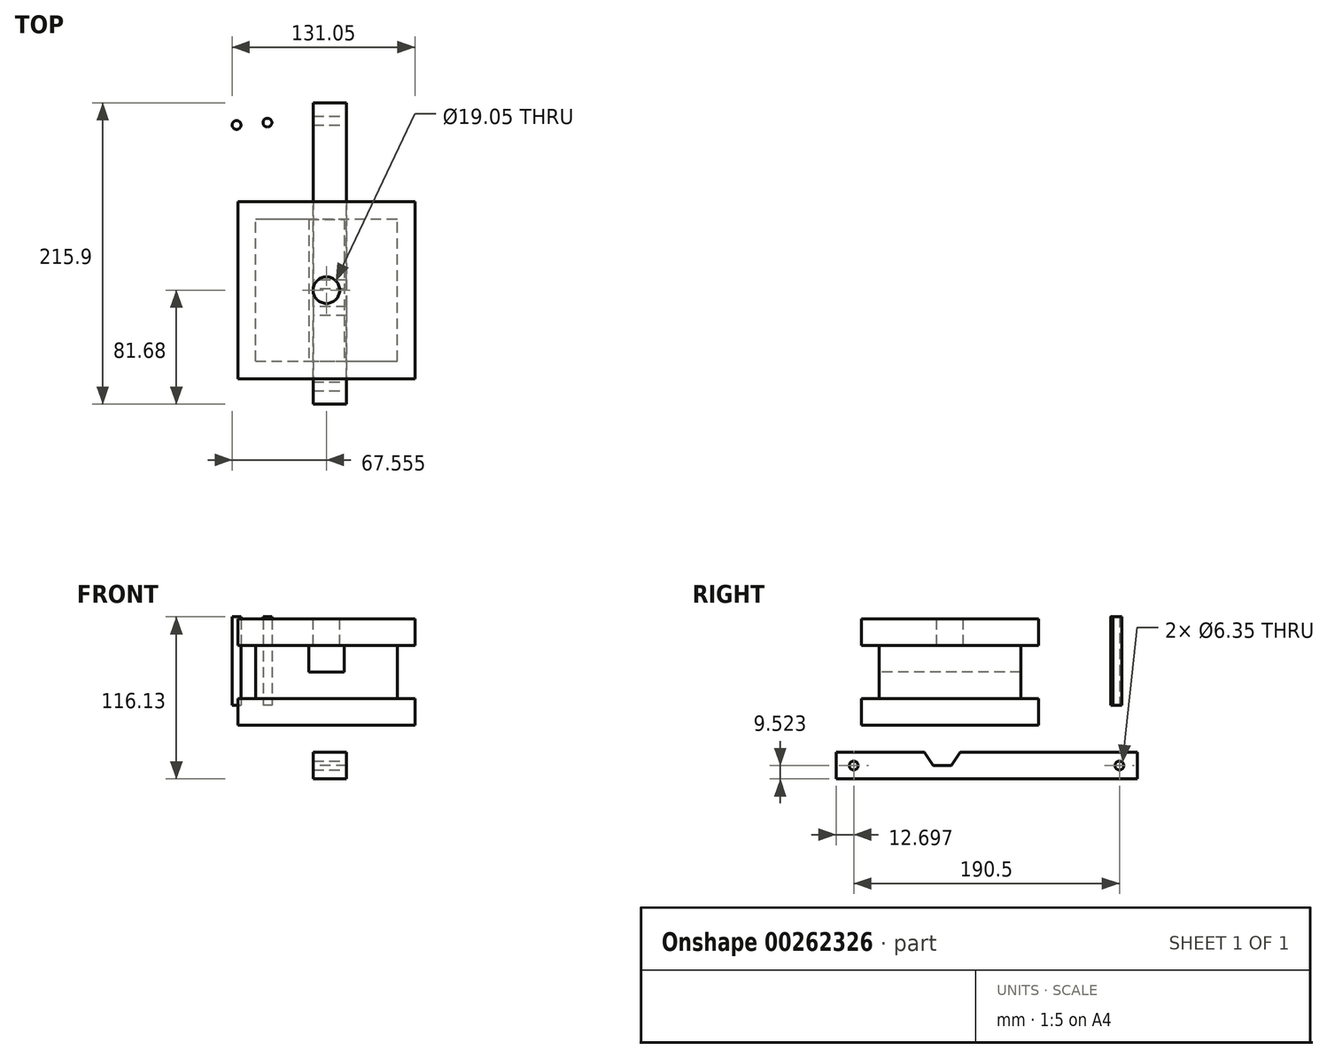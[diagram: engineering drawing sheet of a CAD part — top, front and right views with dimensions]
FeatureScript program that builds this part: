
annotation { "Feature Type Name" : "Feature", "Feature Type Description" : "" }
export const myFeature = defineFeature(function(context is Context, id is Id, definition is map)
    precondition{}
    {
        {
            var Q0;
            Q0=qCreatedBy(makeId("Front.planeOp"),FACE);
            var sketch = newSketch(context, id + "F0", { "sketchPlane" : qUnion([Q0])});
            skLineSegment(sketch, "E0", {"start": v(-54.17, 62.06) * mm, "end": v(72.83, 62.06) * mm});
            skLineSegment(sketch, "E1", {"start": v(72.83, 62.06) * mm, "end": v(72.83, 43) * mm});
            skLineSegment(sketch, "E2", {"start": v(72.83, 4.9) * mm, "end": v(72.83, -14.14) * mm});
            skLineSegment(sketch, "E3", {"start": v(72.83, -14.14) * mm, "end": v(-54.17, -14.14) * mm});
            skLineSegment(sketch, "E4", {"start": v(-54.17, -14.14) * mm, "end": v(-54.17, 4.9) * mm});
            skLineSegment(sketch, "E5", {"start": v(-54.17, 43) * mm, "end": v(-54.17, 62.06) * mm});
            skPoint(sketch, "E6.start.orphan", {"position": v(47.43, 4.9) * mm});
            skLineSegment(sketch, "E7", {"start": v(-54.17, 43) * mm, "end": v(-41.47, 43) * mm});
            skLineSegment(sketch, "E8", {"start": v(-41.47, 43) * mm, "end": v(-41.47, 4.9) * mm});
            skLineSegment(sketch, "E9", {"start": v(-41.47, 4.9) * mm, "end": v(-54.17, 4.9) * mm});
            skLineSegment(sketch, "E10", {"start": v(72.83, 43) * mm, "end": v(60.13, 43) * mm});
            skLineSegment(sketch, "E11", {"start": v(60.13, 43) * mm, "end": v(60.13, 4.9) * mm});
            skLineSegment(sketch, "E12", {"start": v(60.13, 4.9) * mm, "end": v(72.83, 4.9) * mm});
            skSolve(sketch);
        }
        {
            var Q0;
            Q0=makeQuery(id+"F0.imprint","IMPRINT",FACE,{"disambiguationData":[TD([[makeQuery(id+"F0.imprint","IMPRINT",EDGE,{"derivedFrom":sQuery(id+"F0.wireOp",EDGE,"E0")}),-1.0]])]});
            extrude(context, id + "F1", {"entities" : qUnion([Q0]), "depth" : 127 * mm});
        }
        {
            var Q0;
            Q0=makeQuery(id+"F1.opExtrude","CAP_FACE",FACE,{"disambiguationData":[OSD([sQuery(id+"F0.wireOp",EDGE,"E0"),sQuery(id+"F0.wireOp",EDGE,"E1"),sQuery(id+"F0.wireOp",EDGE,"E2"),sQuery(id+"F0.wireOp",EDGE,"E3"),sQuery(id+"F0.wireOp",EDGE,"E4"),sQuery(id+"F0.wireOp",EDGE,"E5"),sQuery(id+"F0.wireOp",EDGE,"E7"),sQuery(id+"F0.wireOp",EDGE,"E8"),sQuery(id+"F0.wireOp",EDGE,"E9"),sQuery(id+"F0.wireOp",EDGE,"E10"),sQuery(id+"F0.wireOp",EDGE,"E11"),sQuery(id+"F0.wireOp",EDGE,"E12")])],"isStart":false});
            var sketch = newSketch(context, id + "F2", { "sketchPlane" : qUnion([Q0])});
            skLineSegment(sketch, "E13", {"start": v(-41.47, 43) * mm, "end": v(60.13, 43) * mm});
            skLineSegment(sketch, "E14", {"start": v(-41.47, 4.9) * mm, "end": v(60.13, 4.9) * mm});
            skSolve(sketch);
        }
        {
            var Q0;
            Q0=makeQuery(id+"F2.imprint","IMPRINT",FACE,{"disambiguationData":[TD([[makeQuery(id+"F2.imprint","IMPRINT",EDGE,{"derivedFrom":sQuery(id+"F2.wireOp",EDGE,"E13")}),-1.0]])]});
            extrude(context, id + "F3", {"entities" : qUnion([Q0]), "operationType" : NewBodyOperationType.REMOVE, "oppositeDirection" : true, "depth" : 12.7 * mm});
        }
        {
            var Q0;
            Q0=makeQuery(id+"F1.opExtrude","CAP_FACE",FACE,{"disambiguationData":[OSD([sQuery(id+"F0.wireOp",EDGE,"E0"),sQuery(id+"F0.wireOp",EDGE,"E1"),sQuery(id+"F0.wireOp",EDGE,"E2"),sQuery(id+"F0.wireOp",EDGE,"E3"),sQuery(id+"F0.wireOp",EDGE,"E4"),sQuery(id+"F0.wireOp",EDGE,"E5"),sQuery(id+"F0.wireOp",EDGE,"E7"),sQuery(id+"F0.wireOp",EDGE,"E8"),sQuery(id+"F0.wireOp",EDGE,"E9"),sQuery(id+"F0.wireOp",EDGE,"E10"),sQuery(id+"F0.wireOp",EDGE,"E11"),sQuery(id+"F0.wireOp",EDGE,"E12")])],"isStart":true});
            var sketch = newSketch(context, id + "F4", { "sketchPlane" : qUnion([Q0])});
            skLineSegment(sketch, "E15", {"start": v(-60.13, 43) * mm, "end": v(41.47, 43) * mm});
            skLineSegment(sketch, "E16", {"start": v(-60.13, 4.9) * mm, "end": v(41.47, 4.9) * mm});
            skSolve(sketch);
        }
        {
            var Q0;
            Q0=makeQuery(id+"F4.imprint","IMPRINT",FACE,{"disambiguationData":[TD([[makeQuery(id+"F4.imprint","IMPRINT",EDGE,{"derivedFrom":sQuery(id+"F4.wireOp",EDGE,"E15")}),-1.0]])]});
            extrude(context, id + "F5", {"entities" : qUnion([Q0]), "operationType" : NewBodyOperationType.REMOVE, "oppositeDirection" : true, "depth" : 12.7 * mm});
        }
        {
            var Q0;
            Q0=makeQuery(id+"F3.boolean.opBoolean","COPY",FACE,{"derivedFrom":makeQuery(id+"F3.opExtrude","CAP_FACE",FACE,{"disambiguationData":[OSD([sQuery(id+"F0.wireOp",EDGE,"E8"),sQuery(id+"F0.wireOp",EDGE,"E11"),sQuery(id+"F2.wireOp",EDGE,"E13"),sQuery(id+"F2.wireOp",EDGE,"E14")])],"isStart":false})});
            var sketch = newSketch(context, id + "F6", { "sketchPlane" : qUnion([Q0])});
            skLineSegment(sketch, "E17", {"start": v(-3.37, 23.96) * mm, "end": v(22.03, 23.96) * mm});
            skLineSegment(sketch, "E18", {"start": v(-3.37, 23.96) * mm, "end": v(-3.37, 43) * mm});
            skLineSegment(sketch, "E19", {"start": v(22.03, 23.96) * mm, "end": v(22.03, 43) * mm});
            skPoint(sketch, "E20.end.orphan", {"position": v(60.13, 23.96) * mm});
            skSolve(sketch);
        }
        {
            var Q0;
            Q0=makeQuery(id+"F6.imprint","IMPRINT",FACE,{"disambiguationData":[TD([[makeQuery(id+"F6.imprint","IMPRINT",EDGE,{"derivedFrom":sQuery(id+"F6.wireOp",EDGE,"E17")}),1.0]])]});
            extrude(context, id + "F7", {"entities" : qUnion([Q0]), "operationType" : NewBodyOperationType.REMOVE, "oppositeDirection" : true, "depth" : 101.6 * mm});
        }
        {
            var Q0;
            Q0=makeQuery(id+"F1.opExtrude","SWEPT_FACE",FACE,{"disambiguationData":[OSD([sQuery(id+"F0.wireOp",EDGE,"E0")])]});
            var sketch = newSketch(context, id + "F8", { "sketchPlane" : qUnion([Q0])});
            skCircle(sketch, "E21", {"center": v(9.33, -63.5) * mm, "radius": 9.53 * mm});
            skPoint(sketch, "E22.orphan", {"position": v(-54.17, -63.5) * mm});
            skPoint(sketch, "E23.orphan", {"position": v(9.33, -127) * mm});
            skPoint(sketch, "E24.orphan", {"position": v(9.33, 0) * mm});
            skPoint(sketch, "E25.start.orphan", {"position": v(72.83, -63.5) * mm});
            skSolve(sketch);
        }
        {
            var Q0;
            Q0=makeQuery(id+"F8.imprint","IMPRINT",FACE,{"disambiguationData":[TD([[makeQuery(id+"F8.imprint","IMPRINT",EDGE,{"derivedFrom":sQuery(id+"F8.wireOp",EDGE,"E21")}),1.0]])]});
            extrude(context, id + "F9", {"entities" : qUnion([Q0]), "operationType" : NewBodyOperationType.REMOVE, "oppositeDirection" : true, "depth" : 25.4 * mm});
        }
        {
            var Q0;
            Q0=qCreatedBy(makeId("Right.planeOp"),FACE);
            var sketch = newSketch(context, id + "F10", { "sketchPlane" : qUnion([Q0])});
            skLineSegment(sketch, "E26", {"start": v(70.72, -33.58) * mm, "end": v(70.72, -52.63) * mm});
            skLineSegment(sketch, "E27", {"start": v(70.72, -52.63) * mm, "end": v(-145.18, -52.63) * mm});
            skLineSegment(sketch, "E28", {"start": v(-145.18, -52.63) * mm, "end": v(-145.18, -33.58) * mm});
            skPoint(sketch, "E29.endSnap0", {"position": v(70.72, -43.1) * mm});
            skPoint(sketch, "E30.start.orphan", {"position": v(-62.63, -43.1) * mm});
            skPoint(sketch, "E31.end.orphan", {"position": v(-81.68, -43.1) * mm});
            skPoint(sketch, "E32.end.orphan", {"position": v(-81.68, -33.58) * mm});
            skLineSegment(sketch, "E33", {"start": v(-145.18, -33.58) * mm, "end": v(-81.68, -33.58) * mm});
            skLineSegment(sketch, "E34", {"start": v(-56.28, -33.58) * mm, "end": v(70.72, -33.58) * mm});
            skLineSegment(sketch, "E35", {"start": v(-75.33, -43.1) * mm, "end": v(-62.63, -43.1) * mm});
            skLineSegment(sketch, "E36", {"start": v(-62.63, -43.1) * mm, "end": v(-56.28, -33.58) * mm});
            skLineSegment(sketch, "E37", {"start": v(-75.33, -43.1) * mm, "end": v(-81.68, -33.58) * mm});
            skPoint(sketch, "E38.start.orphan", {"position": v(-56.28, -43.1) * mm});
            skPoint(sketch, "E39.end.orphan", {"position": v(-56.28, -52.63) * mm});
            skSolve(sketch);
        }
        {
            var Q0;
            Q0=makeQuery(id+"F10.imprint","IMPRINT",FACE,{"disambiguationData":[TD([[makeQuery(id+"F10.imprint","IMPRINT",EDGE,{"derivedFrom":sQuery(id+"F10.wireOp",EDGE,"E26")}),-1.0]])]});
            extrude(context, id + "F11", {"entities" : qUnion([Q0]), "depth" : 23.8 * mm});
        }
        {
            var Q0;
            Q0=qCreatedBy(makeId("Top.planeOp"),FACE);
            var sketch = newSketch(context, id + "F12", { "sketchPlane" : qUnion([Q0])});
            skCircle(sketch, "E40", {"center": v(-55.04, 54.9) * mm, "radius": 3.18 * mm});
            skCircle(sketch, "E41", {"center": v(-32.92, 56.6) * mm, "radius": 3.18 * mm});
            skSolve(sketch);
        }
        {
            var Q0;
            Q0 = qSketchRegion(id + "F12", true);
            extrude(context, id + "F13", {"entities" : qUnion([Q0]), "depth" : 63.5 * mm});
        }
        {
            var Q0;
            Q0=makeQuery(id+"F11.opExtrude","CAP_FACE",FACE,{"disambiguationData":[OSD([sQuery(id+"F10.wireOp",EDGE,"E26"),sQuery(id+"F10.wireOp",EDGE,"E27"),sQuery(id+"F10.wireOp",EDGE,"E28"),sQuery(id+"F10.wireOp",EDGE,"1qvW3he0-5dSp-wWWJ-RM80-zXi0CME8TYfh"),sQuery(id+"F10.wireOp",EDGE,"SPbg9B3L-6TkF-tD2P-HhvK-yeJ9XdwqM4mz"),sQuery(id+"F10.wireOp",EDGE,"S64I6AJy-TqXl-azHu-CEL1-guYVQ2bvu08o"),sQuery(id+"F10.wireOp",EDGE,"tNPECCfJ-GeBg-PJKQ-abuN-mUDomsZt7gyD"),sQuery(id+"F10.wireOp",EDGE,"f4980219-b4c7-42b5-b36a-03a1228a95d6.trimOffspring")])],"isStart":false});
            var sketch = newSketch(context, id + "F14", { "sketchPlane" : qUnion([Q0])});
            skCircle(sketch, "E42", {"center": v(-132.48, -43.1) * mm, "radius": 3.18 * mm});
            skCircle(sketch, "E43", {"center": v(58.02, -43.1) * mm, "radius": 3.18 * mm});
            skPoint(sketch, "E44.orphan", {"position": v(-145.18, -43.1) * mm});
            skPoint(sketch, "E45.orphan", {"position": v(70.72, -43.1) * mm});
            skSolve(sketch);
        }
        {
            var Q0;
            Q0=makeQuery(id+"F14.imprint","IMPRINT",FACE,{"disambiguationData":[TD([[makeQuery(id+"F14.imprint","IMPRINT",EDGE,{"derivedFrom":sQuery(id+"F14.wireOp",EDGE,"E42")}),1.0]])]});
            var Q1;
            Q1=makeQuery(id+"F14.imprint","IMPRINT",FACE,{"disambiguationData":[TD([[makeQuery(id+"F14.imprint","IMPRINT",EDGE,{"derivedFrom":sQuery(id+"F14.wireOp",EDGE,"E43")}),1.0]])]});
            extrude(context, id + "F15", {"entities" : qUnion([Q0, Q1]), "operationType" : NewBodyOperationType.REMOVE, "oppositeDirection" : true, "depth" : 25.4 * mm});
        }
    });
